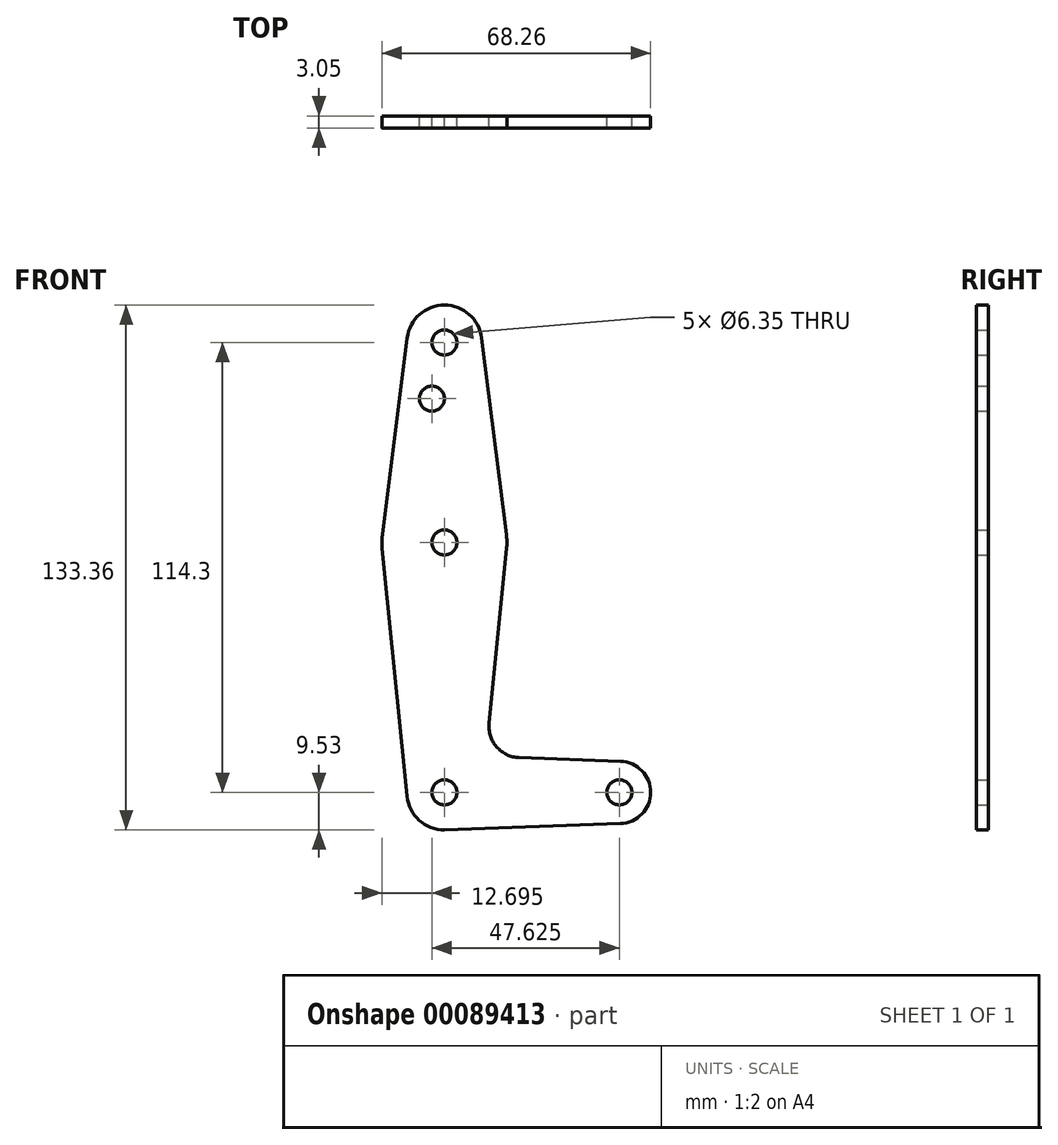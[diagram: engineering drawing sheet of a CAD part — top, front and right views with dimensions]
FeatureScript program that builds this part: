
annotation { "Feature Type Name" : "Feature", "Feature Type Description" : "" }
export const myFeature = defineFeature(function(context is Context, id is Id, definition is map)
    precondition{}
    {
        {
            var Q0;
            Q0=qCreatedBy(makeId("Front.planeOp"),FACE);
            var sketch = newSketch(context, id + "F0", { "sketchPlane" : qUnion([Q0])});
            skLineSegment(sketch, "E0", {"start": v(0, 114.3) * mm, "end": v(0, 0) * mm, "construction": true});
            skLineSegment(sketch, "E1", {"start": v(0, 0) * mm, "end": v(44.45, 0) * mm, "construction": true});
            skCircle(sketch, "E2", {"center": v(0, 114.3) * mm, "radius": 9.52 * mm});
            skCircle(sketch, "E3", {"center": v(0, 63.5) * mm, "radius": 15.88 * mm});
            skCircle(sketch, "E4", {"center": v(0, 0) * mm, "radius": 9.53 * mm});
            skCircle(sketch, "E5", {"center": v(44.45, 0) * mm, "radius": 7.94 * mm});
            skLineSegment(sketch, "E6", {"start": v(15.8, 61.91) * mm, "end": v(11.34, 17.59) * mm});
            skLineSegment(sketch, "E7", {"start": v(0, -9.53) * mm, "end": v(44.73, -7.93) * mm});
            skLineSegment(sketch, "E8", {"start": v(18.97, 8.85) * mm, "end": v(44.73, 7.93) * mm});
            skCircle(sketch, "E9", {"center": v(0, 114.3) * mm, "radius": 3.18 * mm});
            skCircle(sketch, "E10", {"center": v(-3.18, 100.03) * mm, "radius": 3.18 * mm});
            skCircle(sketch, "E11", {"center": v(44.45, 0) * mm, "radius": 3.18 * mm});
            skCircle(sketch, "E12", {"center": v(0, 0) * mm, "radius": 3.18 * mm});
            skPoint(sketch, "E13.newPointB", {"position": v(0, 9.53) * mm});
            skArc(sketch, "E13.filletArc", {"start": v(11.34, 17.59) * mm, "mid": v(13.26, 11.57) * mm, "end": v(18.97, 8.85) * mm});
            skCircle(sketch, "E14", {"center": v(0, 63.5) * mm, "radius": 3.18 * mm});
            skLineSegment(sketch, "E15", {"start": v(-9.45, 115.5) * mm, "end": v(-15.75, 65.48) * mm});
            skLineSegment(sketch, "E16", {"start": v(9.45, 115.5) * mm, "end": v(15.75, 65.48) * mm});
            skLineSegment(sketch, "E17", {"start": v(-15.8, 61.91) * mm, "end": v(-9.48, -0.95) * mm});
            skSolve(sketch);
        }
        {
            var Q0;
            Q0=makeQuery(id+"F0.imprint","IMPRINT",FACE,{"disambiguationData":[TD([[makeQuery(id+"F0.imprint","IMPRINT",EDGE,{"derivedFrom":sQuery(id+"F0.wireOp",EDGE,"E10")}),-1.0]])]});
            var Q1;
            Q1=makeQuery(id+"F0.imprint","IMPRINT",FACE,{"disambiguationData":[TD([[makeQuery(id+"F0.imprint","IMPRINT",EDGE,{"derivedFrom":sQuery(id+"F0.wireOp",EDGE,"E9")}),-1.0]])]});
            var Q2;
            Q2=makeQuery(id+"F0.imprint","IMPRINT",FACE,{"disambiguationData":[TD([[makeQuery(id+"F0.imprint","IMPRINT",EDGE,{"derivedFrom":sQuery(id+"F0.wireOp",EDGE,"E14")}),-1.0]])]});
            var Q3;
            {var subQ0=sQuery(id+"F0.wireOp",EDGE,"E6");Q3=makeQuery(id+"F0.imprint","IMPRINT",FACE,{"disambiguationData":[TD([[makeQuery(id+"F0.imprint","IMPRINT",EDGE,{"derivedFrom":subQ0}),-1.0]])]});}
            var Q4;
            Q4=makeQuery(id+"F0.imprint","IMPRINT",FACE,{"disambiguationData":[TD([[makeQuery(id+"F0.imprint","IMPRINT",EDGE,{"derivedFrom":sQuery(id+"F0.wireOp",EDGE,"E12")}),-1.0]])]});
            var Q5;
            Q5=makeQuery(id+"F0.imprint","IMPRINT",FACE,{"disambiguationData":[TD([[makeQuery(id+"F0.imprint","IMPRINT",EDGE,{"derivedFrom":sQuery(id+"F0.wireOp",EDGE,"E11")}),-1.0]])]});
            extrude(context, id + "F1", {"entities" : qUnion([Q0, Q1, Q2, Q3, Q4, Q5]), "depth" : 3.05 * mm});
        }
    });
